# Revit family: Sink-Undermount-Lavatory-KOHLER-Ladena-K-36402PH
name_source: partatom
category: Plumbing Fixtures
units: mm (PartAtom-declared; Revit-internal decimal feet)

## family parameters
Cut with Voids When Loaded = No
Host = Face
Maintain Annotation Orientation = No
OmniClass Number = 23.31.13.00
Part Type = Normal
Room Calculation Point = No
Round Connector Dimension = Use Diameter
Shared = No

## types (3) — shared parameters
ADA Compliant = No
Assembly Code = D2010400
CW Connection = No
Cold Water Inlet = Cold Water Inlet
Date Modified = 03/24/2025
Default Elevation = 36"
Description = Refresh Under Counter Reactangular 530 mm
Drain Included = No
HW Connection = No
Height = 8 3/8"
Hot Water Inlet = Hot Water Inlet
Length = 15 5/8"
Manufacturer = Kohler Co.
Master Format 2014 = 22 41 16
Master Format 2014 Name = Residential Lavatories and Sinks
Material = Viterous China
Product Name = Ladena
URL = https://www.kohler.ph
Vent Connection = No
Waste Connection = Yes
Waste Water Outlet = Waste Water Outlet
WaterSense Certified = No
Width = 22 13/16"

## per-type parameters (varying)
| type | Finish | Model | Type |
| 0-White | Kohler-Vitreous_China-0-White | K-36402PH-0 | 1 |
| HB1-Honed Black | Kohler-Vitreous_China-HB1-Honed_Black | K-36402PH-HB1 | 2 |
| TRF-Truffle | KOHLER-Vitreous_China-TRF-Truffle | K-36402PH-TRF | 3 |

## geometry (parser evidence)
native form markers: Sweep x5
no freeform markers — native parametric forms only
